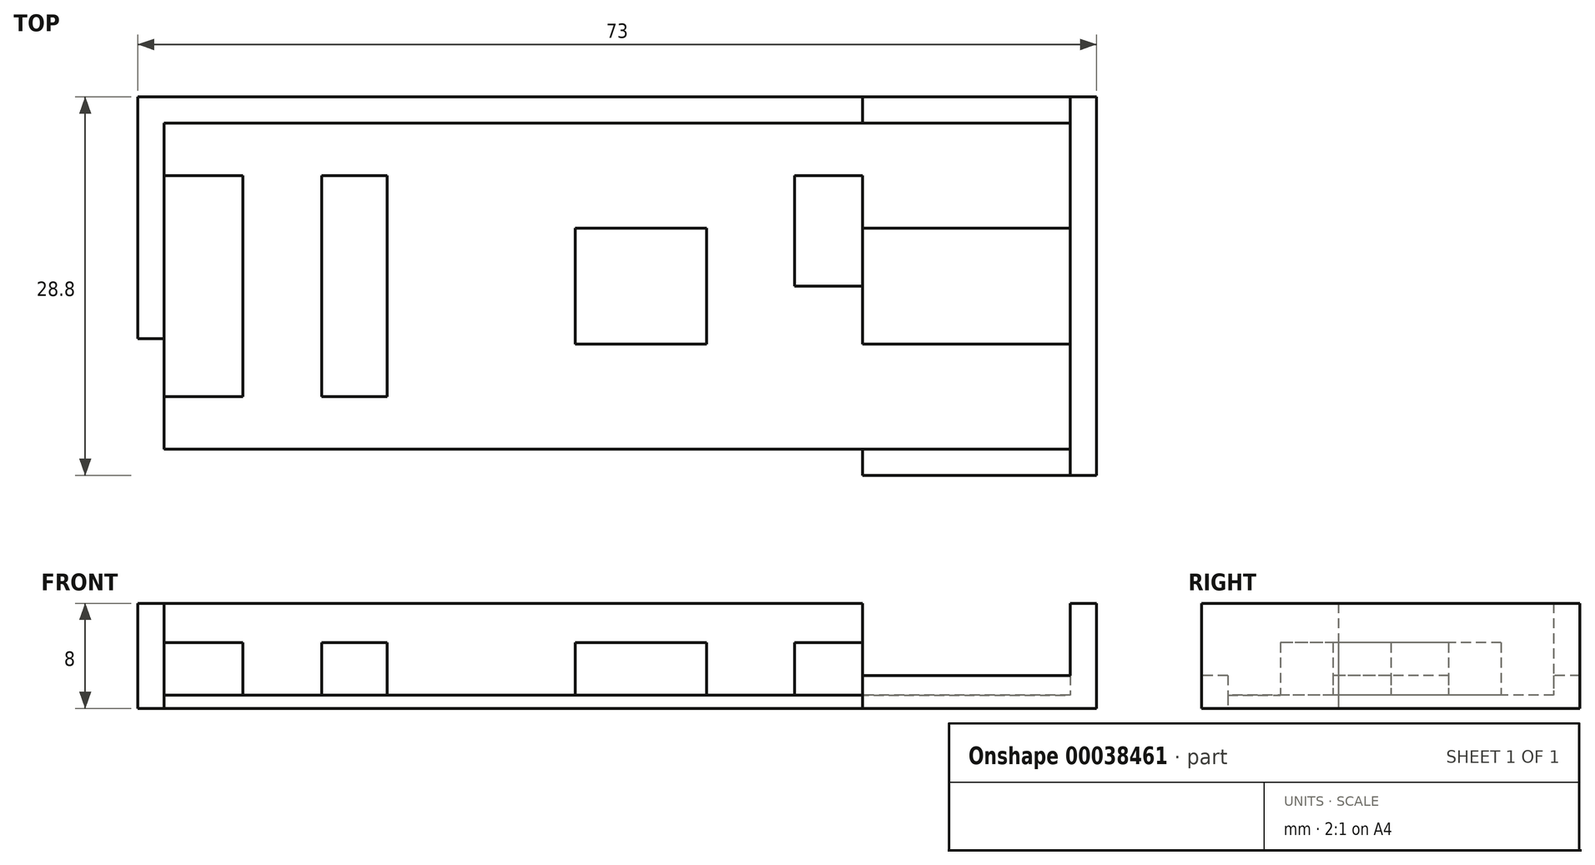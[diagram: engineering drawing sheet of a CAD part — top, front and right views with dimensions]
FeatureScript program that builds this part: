
annotation { "Feature Type Name" : "Feature", "Feature Type Description" : "" }
export const myFeature = defineFeature(function(context is Context, id is Id, definition is map)
    precondition{}
    {
        {
            var Q0;
            Q0=qCreatedBy(makeId("Top.planeOp"),FACE);
            var sketch = newSketch(context, id + "F0", { "sketchPlane" : qUnion([Q0])});
            skLineSegment(sketch, "E0", {"start": v(0, 4) * mm, "end": v(64, 4) * mm, "construction": true});
            skLineSegment(sketch, "E1", {"start": v(0, 20.8) * mm, "end": v(53.2, 20.8) * mm, "construction": true});
            skLineSegment(sketch, "E2", {"start": v(41.3, 20.8) * mm, "end": v(41.3, 4) * mm, "construction": true});
            skLineSegment(sketch, "E3.bottom", {"start": v(41.3, 16.8) * mm, "end": v(31.3, 16.8) * mm});
            skLineSegment(sketch, "E3.top", {"start": v(41.3, 8) * mm, "end": v(31.3, 8) * mm});
            skLineSegment(sketch, "E3.left", {"start": v(41.3, 16.8) * mm, "end": v(41.3, 8) * mm});
            skLineSegment(sketch, "E3.right", {"start": v(31.3, 16.8) * mm, "end": v(31.3, 8) * mm});
            skLineSegment(sketch, "E4.bottom", {"start": v(0, 20.8) * mm, "end": v(6, 20.8) * mm});
            skLineSegment(sketch, "E4.top", {"start": v(0, 4) * mm, "end": v(6, 4) * mm});
            skLineSegment(sketch, "E4.right", {"start": v(6, 20.8) * mm, "end": v(6, 4) * mm});
            skLineSegment(sketch, "E5.bottom", {"start": v(12, 20.8) * mm, "end": v(17, 20.8) * mm});
            skLineSegment(sketch, "E5.top", {"start": v(12, 4) * mm, "end": v(17, 4) * mm});
            skLineSegment(sketch, "E5.left", {"start": v(12, 20.8) * mm, "end": v(12, 4) * mm});
            skLineSegment(sketch, "E5.right", {"start": v(17, 20.8) * mm, "end": v(17, 4) * mm});
            skLineSegment(sketch, "E6.bottom", {"start": v(48, 20.8) * mm, "end": v(53.2, 20.8) * mm});
            skLineSegment(sketch, "E6.top", {"start": v(48, 12.4) * mm, "end": v(53.2, 12.4) * mm});
            skLineSegment(sketch, "E6.left", {"start": v(48, 20.8) * mm, "end": v(48, 12.4) * mm});
            skLineSegment(sketch, "E7", {"start": v(53.2, 50.95) * mm, "end": v(53.2, -26.15) * mm, "construction": true});
            skLineSegment(sketch, "E8", {"start": v(69, 59.43) * mm, "end": v(69, -48.28) * mm, "construction": true});
            skLineSegment(sketch, "E9", {"start": v(0, 53.08) * mm, "end": v(0, -48) * mm, "construction": true});
            skLineSegment(sketch, "E10", {"start": v(71, 54.69) * mm, "end": v(71, -59.79) * mm, "construction": true});
            skLineSegment(sketch, "E11", {"start": v(-24.24, -2) * mm, "end": v(101.32, -2) * mm, "construction": true});
            skLineSegment(sketch, "E12", {"start": v(-27.25, 26.8) * mm, "end": v(95.05, 26.8) * mm, "construction": true});
            skLineSegment(sketch, "E13", {"start": v(-2, 53.72) * mm, "end": v(-2, -68.22) * mm, "construction": true});
            skLineSegment(sketch, "E14", {"start": v(-39.18, 24.8) * mm, "end": v(95.54, 24.8) * mm, "construction": true});
            skLineSegment(sketch, "E15.left", {"start": v(0, 20.8) * mm, "end": v(0, 4) * mm});
            skLineSegment(sketch, "E16", {"start": v(53.2, 20.8) * mm, "end": v(53.2, 12.4) * mm});
            skLineSegment(sketch, "E17.bottom", {"start": v(69, 26.8) * mm, "end": v(71, 26.8) * mm});
            skLineSegment(sketch, "E17.top", {"start": v(69, -2) * mm, "end": v(71, -2) * mm});
            skLineSegment(sketch, "E17.left", {"start": v(69, 26.8) * mm, "end": v(69, -2) * mm});
            skLineSegment(sketch, "E17.right", {"start": v(71, 26.8) * mm, "end": v(71, -2) * mm});
            skLineSegment(sketch, "E18", {"start": v(83.68, 8) * mm, "end": v(51.38, 8) * mm, "construction": true});
            skLineSegment(sketch, "E19", {"start": v(82.66, 16.8) * mm, "end": v(49.28, 16.8) * mm, "construction": true});
            skLineSegment(sketch, "E20.bottom", {"start": v(53.2, 26.8) * mm, "end": v(69, 26.8) * mm});
            skLineSegment(sketch, "E20.top", {"start": v(53.2, 24.8) * mm, "end": v(69, 24.8) * mm});
            skLineSegment(sketch, "E20.left", {"start": v(53.2, 26.8) * mm, "end": v(53.2, 24.8) * mm});
            skLineSegment(sketch, "E20.right", {"start": v(69, 26.8) * mm, "end": v(69, 24.8) * mm});
            skLineSegment(sketch, "E21.top", {"start": v(53.2, 16.8) * mm, "end": v(69, 16.8) * mm});
            skLineSegment(sketch, "E21.left", {"start": v(53.2, 24.8) * mm, "end": v(53.2, 16.8) * mm});
            skLineSegment(sketch, "E21.right", {"start": v(69, 24.8) * mm, "end": v(69, 16.8) * mm});
            skLineSegment(sketch, "E22.top", {"start": v(53.2, 8) * mm, "end": v(69, 8) * mm});
            skLineSegment(sketch, "E22.left", {"start": v(53.2, 16.8) * mm, "end": v(53.2, 8) * mm});
            skLineSegment(sketch, "E22.right", {"start": v(69, 16.8) * mm, "end": v(69, 8) * mm});
            skLineSegment(sketch, "E23.top", {"start": v(53.2, 0) * mm, "end": v(69, 0) * mm});
            skLineSegment(sketch, "E23.left", {"start": v(53.2, 8) * mm, "end": v(53.2, 0) * mm});
            skLineSegment(sketch, "E23.right", {"start": v(69, 8) * mm, "end": v(69, 0) * mm});
            skLineSegment(sketch, "E24.top", {"start": v(53.2, -2) * mm, "end": v(69, -2) * mm});
            skLineSegment(sketch, "E24.left", {"start": v(53.2, 0) * mm, "end": v(53.2, -2) * mm});
            skLineSegment(sketch, "E24.right", {"start": v(69, 0) * mm, "end": v(69, -2) * mm});
            skLineSegment(sketch, "E25", {"start": v(53.2, 26.8) * mm, "end": v(-2, 26.8) * mm});
            skLineSegment(sketch, "E26", {"start": v(53.2, 24.8) * mm, "end": v(0, 24.8) * mm});
            skLineSegment(sketch, "E27", {"start": v(-8.82, 12.4) * mm, "end": v(3.3, 12.4) * mm, "construction": true});
            skLineSegment(sketch, "E28.bottom", {"start": v(-2, 16.4) * mm, "end": v(0, 16.4) * mm});
            skLineSegment(sketch, "E28.top", {"start": v(-2, 8.4) * mm, "end": v(0, 8.4) * mm});
            skLineSegment(sketch, "E28.left", {"start": v(-2, 16.4) * mm, "end": v(-2, 8.4) * mm});
            skLineSegment(sketch, "E28.right", {"start": v(0, 16.4) * mm, "end": v(0, 8.4) * mm});
            skLineSegment(sketch, "E29", {"start": v(0, 24.8) * mm, "end": v(0, 16.4) * mm});
            skLineSegment(sketch, "E30", {"start": v(-2, 16.4) * mm, "end": v(-2, 26.8) * mm});
            skLineSegment(sketch, "E31", {"start": v(-2, 8.4) * mm, "end": v(-2, -2) * mm});
            skLineSegment(sketch, "E32", {"start": v(-2, -2) * mm, "end": v(53.2, -2) * mm});
            skLineSegment(sketch, "E33", {"start": v(53.2, 0) * mm, "end": v(0, 0) * mm});
            skLineSegment(sketch, "E34", {"start": v(0, 0) * mm, "end": v(0, 4) * mm});
            skSolve(sketch);
        }
        {
            var Q0;
            {var subQ3=sQuery(id+"F0.wireOp",EDGE,"E20.top");Q0=makeQuery(id+"F0.imprint","IMPRINT",FACE,{"disambiguationData":[TD([[makeQuery(id+"F0.imprint","IMPRINT",EDGE,{"derivedFrom":subQ3}),-1.0]])]});}
            var Q1;
            Q1=makeQuery(id+"F0.imprint","IMPRINT",FACE,{"disambiguationData":[TD([[makeQuery(id+"F0.imprint","IMPRINT",EDGE,{"derivedFrom":sQuery(id+"F0.wireOp",EDGE,"E3.bottom")}),-1.0]])]});
            var Q2;
            Q2=makeQuery(id+"F0.imprint","IMPRINT",FACE,{"disambiguationData":[TD([[makeQuery(id+"F0.imprint","IMPRINT",EDGE,{"derivedFrom":sQuery(id+"F0.wireOp",EDGE,"E22.top")}),-1.0]])]});
            extrude(context, id + "F1", {"entities" : qUnion([Q0, Q1, Q2]), "depth" : 1 * mm});
        }
        {
            var Q0;
            Q0=makeQuery(id+"F0.imprint","IMPRINT",FACE,{"disambiguationData":[TD([[makeQuery(id+"F0.imprint","IMPRINT",EDGE,{"derivedFrom":sQuery(id+"F0.wireOp",EDGE,"E20.bottom")}),-1.0]])]});
            var Q1;
            {var subQ3=sQuery(id+"F0.wireOp",EDGE,"E21.top");Q1=makeQuery(id+"F0.imprint","IMPRINT",FACE,{"disambiguationData":[TD([[makeQuery(id+"F0.imprint","IMPRINT",EDGE,{"derivedFrom":subQ3}),-1.0]])]});}
            var Q2;
            Q2=makeQuery(id+"F0.imprint","IMPRINT",FACE,{"disambiguationData":[TD([[makeQuery(id+"F0.imprint","IMPRINT",EDGE,{"derivedFrom":sQuery(id+"F0.wireOp",EDGE,"E23.top")}),-1.0]])]});
            extrude(context, id + "F2", {"entities" : qUnion([Q0, Q1, Q2]), "operationType" : NewBodyOperationType.ADD, "depth" : 2.5 * mm});
        }
        {
            var Q0;
            {var subQ0=sQuery(id+"F0.wireOp",EDGE,"E4.bottom");Q0=makeQuery(id+"F0.imprint","IMPRINT",FACE,{"disambiguationData":[TD([[makeQuery(id+"F0.imprint","IMPRINT",EDGE,{"derivedFrom":subQ0}),-1.0]])]});}
            var Q1;
            Q1=makeQuery(id+"F0.imprint","IMPRINT",FACE,{"disambiguationData":[TD([[makeQuery(id+"F0.imprint","IMPRINT",EDGE,{"derivedFrom":sQuery(id+"F0.wireOp",EDGE,"E5.bottom")}),-1.0]])]});
            var Q2;
            Q2=makeQuery(id+"F0.imprint","IMPRINT",FACE,{"disambiguationData":[TD([[makeQuery(id+"F0.imprint","IMPRINT",EDGE,{"derivedFrom":sQuery(id+"F0.wireOp",EDGE,"E3.bottom")}),1.0]])]});
            var Q3;
            {var subQ1=sQuery(id+"F0.wireOp",EDGE,"E6.bottom");Q3=makeQuery(id+"F0.imprint","IMPRINT",FACE,{"disambiguationData":[TD([[makeQuery(id+"F0.imprint","IMPRINT",EDGE,{"derivedFrom":subQ1}),-1.0]])]});}
            extrude(context, id + "F3", {"entities" : qUnion([Q0, Q1, Q2, Q3]), "operationType" : NewBodyOperationType.ADD, "depth" : 5 * mm});
        }
        {
            var Q0;
            Q0=makeQuery(id+"F0.imprint","IMPRINT",FACE,{"disambiguationData":[TD([[makeQuery(id+"F0.imprint","IMPRINT",EDGE,{"derivedFrom":sQuery(id+"F0.wireOp",EDGE,"E25")}),1.0]])]});
            var Q1;
            Q1=makeQuery(id+"F0.imprint","IMPRINT",FACE,{"disambiguationData":[TD([[makeQuery(id+"F0.imprint","IMPRINT",EDGE,{"derivedFrom":sQuery(id+"F0.wireOp",EDGE,"E17.bottom")}),-1.0]])]});
            var Q2;
            Q2=makeQuery(id+"F0.imprint","IMPRINT",FACE,{"disambiguationData":[TD([[makeQuery(id+"F0.imprint","IMPRINT",EDGE,{"derivedFrom":sQuery(id+"F0.wireOp",EDGE,"E15.left")}),-1.0]])]});
            extrude(context, id + "F4", {"entities" : qUnion([Q0, Q1, Q2]), "operationType" : NewBodyOperationType.ADD, "depth" : 8 * mm});
        }
        {
            var Q0;
            Q0=makeQuery(id+"F0.imprint","IMPRINT",FACE,{"disambiguationData":[TD([[makeQuery(id+"F0.imprint","IMPRINT",EDGE,{"derivedFrom":sQuery(id+"F0.wireOp",EDGE,"E28.bottom")}),-1.0]])]});
            extrude(context, id + "F5", {"entities" : qUnion([Q0]), "operationType" : NewBodyOperationType.ADD, "depth" : 6 * mm});
        }
    });
